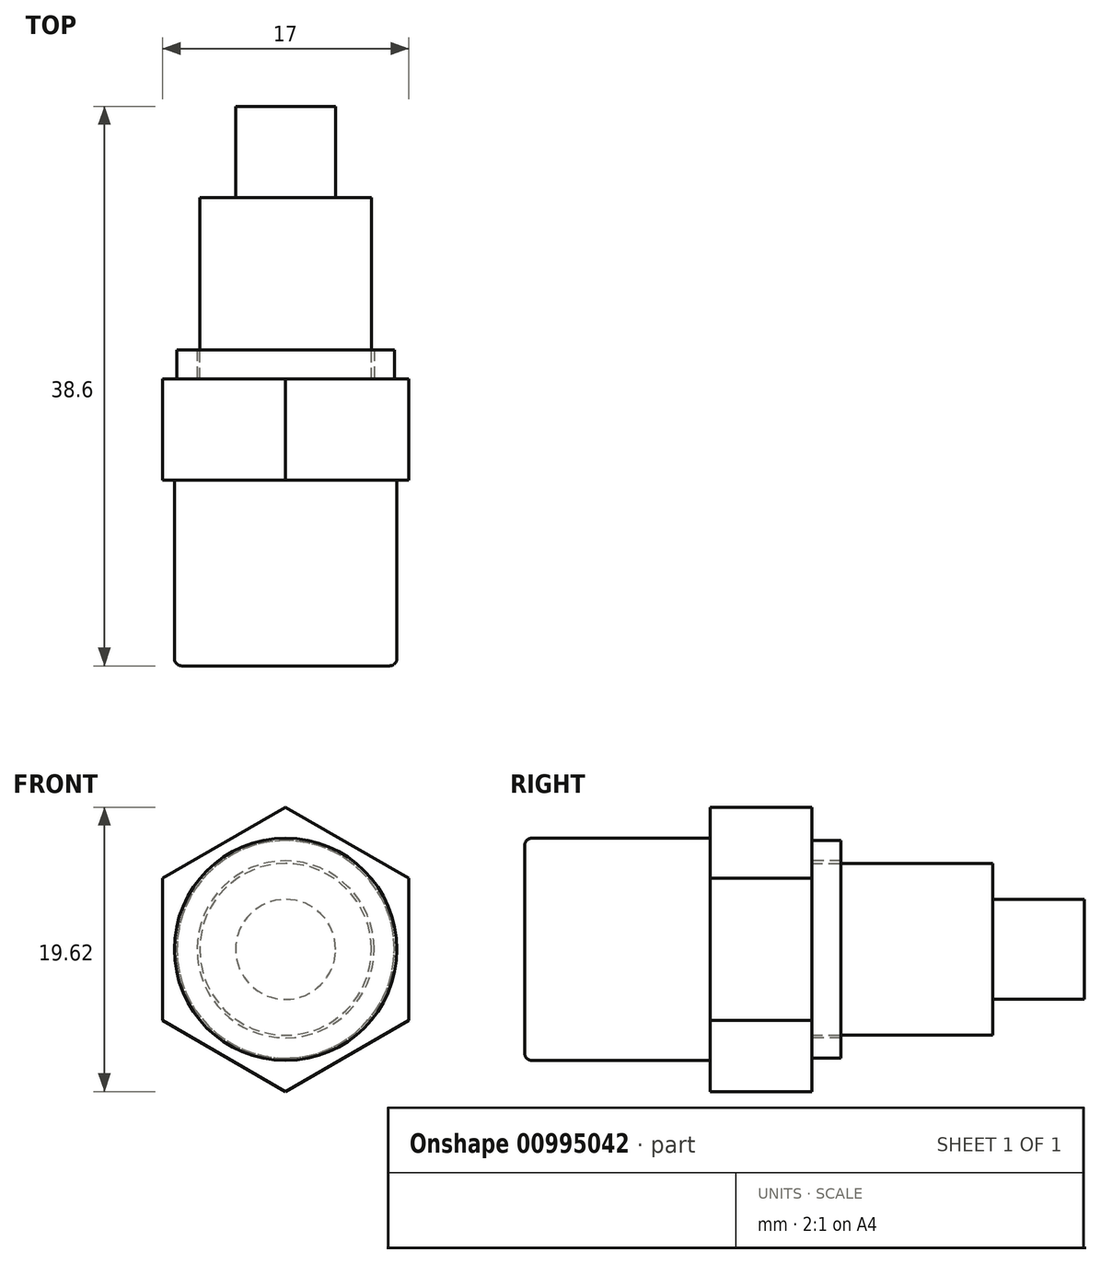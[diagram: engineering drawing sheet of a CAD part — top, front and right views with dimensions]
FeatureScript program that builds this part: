
annotation { "Feature Type Name" : "Feature", "Feature Type Description" : "" }
export const myFeature = defineFeature(function(context is Context, id is Id, definition is map)
    precondition{}
    {
        {
            var Q0;
            Q0=qCreatedBy(makeId("Front.planeOp"),FACE);
            var sketch = newSketch(context, id + "F0", { "sketchPlane" : qUnion([Q0])});
            skCircle(sketch, "E0", {"center": v(0, 0) * mm, "radius": 3.45 * mm});
            skSolve(sketch);
        }
        {
            var Q0;
            Q0 = qSketchRegion(id + "F0", true);
            extrude(context, id + "F1", {"entities" : qUnion([Q0]), "depth" : 6.3 * mm, "offsetDistance" : 25 * mm});
        }
        {
            var Q0;
            Q0=makeQuery(id+"F1.opExtrude","CAP_FACE",FACE,{"disambiguationData":[OSD([sQuery(id+"F0.wireOp",EDGE,"E0")])],"isStart":false});
            var sketch = newSketch(context, id + "F2", { "sketchPlane" : qUnion([Q0])});
            skCircle(sketch, "E1", {"center": v(0, 0) * mm, "radius": 5.92 * mm});
            skSolve(sketch);
        }
        {
            var Q0;
            Q0 = qSketchRegion(id + "F2", true);
            extrude(context, id + "F3", {"entities" : qUnion([Q0]), "operationType" : NewBodyOperationType.ADD, "depth" : 12.5 * mm, "offsetDistance" : 25 * mm});
        }
        {
            var Q0;
            Q0=makeQuery(id+"F3.opExtrude","CAP_FACE",FACE,{"disambiguationData":[OSD([sQuery(id+"F2.wireOp",EDGE,"E1")])],"isStart":false});
            var sketch = newSketch(context, id + "F4", { "sketchPlane" : qUnion([Q0])});
            skCircle(sketch, "E2.cCircle", {"center": v(0, 0) * mm, "radius": 8.5 * mm, "construction": true});
            skLineSegment(sketch, "E2.0", {"start": v(-8.5, 4.9) * mm, "end": v(0, 9.81) * mm});
            skLineSegment(sketch, "E2.1", {"start": v(0, 9.81) * mm, "end": v(8.5, 4.9) * mm});
            skLineSegment(sketch, "E2.2", {"start": v(8.5, 4.9) * mm, "end": v(8.5, -4.9) * mm});
            skLineSegment(sketch, "E2.3", {"start": v(8.5, -4.9) * mm, "end": v(0, -9.81) * mm});
            skLineSegment(sketch, "E2.4", {"start": v(0, -9.81) * mm, "end": v(-8.5, -4.9) * mm});
            skLineSegment(sketch, "E2.5", {"start": v(-8.5, -4.9) * mm, "end": v(-8.5, 4.9) * mm});
            skPoint(sketch, "E2.0.midPoint", {"position": v(-4.25, 7.36) * mm});
            skSolve(sketch);
        }
        {
            var Q0;
            Q0 = qSketchRegion(id + "F4", true);
            extrude(context, id + "F5", {"entities" : qUnion([Q0]), "operationType" : NewBodyOperationType.ADD, "depth" : 7 * mm, "offsetDistance" : 25 * mm});
        }
        {
            var Q0;
            Q0=makeQuery(id+"F5.opExtrude","CAP_FACE",FACE,{"disambiguationData":[OSD([sQuery(id+"F4.wireOp",EDGE,"E2.0"),sQuery(id+"F4.wireOp",EDGE,"E2.1"),sQuery(id+"F4.wireOp",EDGE,"E2.2"),sQuery(id+"F4.wireOp",EDGE,"E2.3"),sQuery(id+"F4.wireOp",EDGE,"E2.4"),sQuery(id+"F4.wireOp",EDGE,"E2.5")])],"isStart":false});
            var sketch = newSketch(context, id + "F6", { "sketchPlane" : qUnion([Q0])});
            skCircle(sketch, "E3", {"center": v(0, 0) * mm, "radius": 7.68 * mm});
            skSolve(sketch);
        }
        {
            var Q0;
            Q0 = qSketchRegion(id + "F6", true);
            extrude(context, id + "F7", {"entities" : qUnion([Q0]), "operationType" : NewBodyOperationType.ADD, "depth" : 12.8 * mm, "offsetDistance" : 25 * mm});
        }
        {
            var Q0;
            Q0=makeQuery(id+"F7.opExtrude","CAP_EDGE",EDGE,{"disambiguationData":[OSD([sQuery(id+"F6.wireOp",EDGE,"E3")])],"isStart":false});
            fillet(context, id + "F8", {"entities" : qUnion([Q0]), "radius" : 0.5 * mm, "tangentPropagation" : true, "allowEdgeOverflow" : false});
        }
        {
            var Q0;
            Q0=makeQuery(id+"F5.opExtrude","CAP_FACE",FACE,{"disambiguationData":[OSD([sQuery(id+"F4.wireOp",EDGE,"E2.0"),sQuery(id+"F4.wireOp",EDGE,"E2.1"),sQuery(id+"F4.wireOp",EDGE,"E2.2"),sQuery(id+"F4.wireOp",EDGE,"E2.3"),sQuery(id+"F4.wireOp",EDGE,"E2.4"),sQuery(id+"F4.wireOp",EDGE,"E2.5")])],"isStart":true});
            var sketch = newSketch(context, id + "F9", { "sketchPlane" : qUnion([Q0])});
            skCircle(sketch, "E4", {"center": v(0, 0) * mm, "radius": 7.5 * mm});
            skCircle(sketch, "E5", {"center": v(0, 0) * mm, "radius": 6.1 * mm});
            skSolve(sketch);
        }
        {
            var Q0;
            Q0 = qSketchRegion(id + "F9", true);
            extrude(context, id + "F10", {"entities" : qUnion([Q0]), "operationType" : NewBodyOperationType.ADD, "depth" : 2 * mm, "offsetDistance" : 25 * mm});
        }
    });
